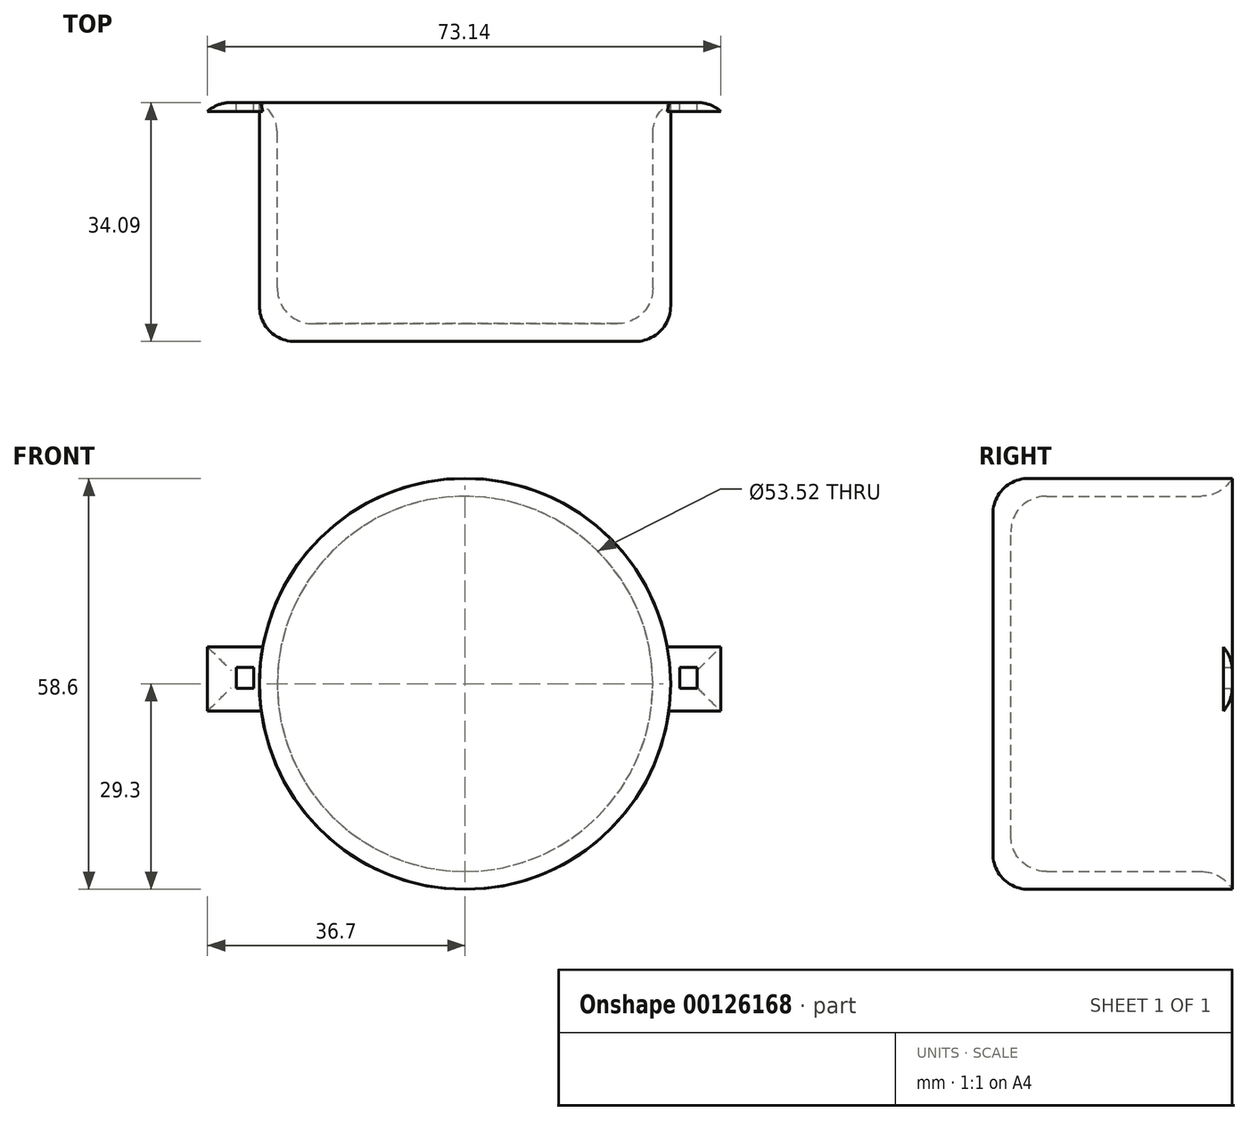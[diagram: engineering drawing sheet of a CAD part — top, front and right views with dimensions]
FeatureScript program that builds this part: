
annotation { "Feature Type Name" : "Feature", "Feature Type Description" : "" }
export const myFeature = defineFeature(function(context is Context, id is Id, definition is map)
    precondition{}
    {
        {
            var Q0;
            Q0=qCreatedBy(makeId("Front.planeOp"),FACE);
            var sketch = newSketch(context, id + "F0", { "sketchPlane" : qUnion([Q0])});
            skCircle(sketch, "E0", {"center": v(0, 0) * mm, "radius": 29.3 * mm});
            skLineSegment(sketch, "E1", {"start": v(28.82, 5.27) * mm, "end": v(36.44, 5.27) * mm});
            skLineSegment(sketch, "E2", {"start": v(36.44, 5.27) * mm, "end": v(36.44, -3.9) * mm});
            skLineSegment(sketch, "E3", {"start": v(36.44, -3.9) * mm, "end": v(29.04, -3.9) * mm});
            skLineSegment(sketch, "E4", {"start": v(-28.82, 5.27) * mm, "end": v(-36.7, 5.27) * mm});
            skLineSegment(sketch, "E5", {"start": v(-36.7, 5.27) * mm, "end": v(-36.7, -3.9) * mm});
            skLineSegment(sketch, "E6", {"start": v(-36.7, -3.9) * mm, "end": v(-29.04, -3.9) * mm});
            skLineSegment(sketch, "E7", {"start": v(30.6, 2.33) * mm, "end": v(30.6, -0.61) * mm});
            skLineSegment(sketch, "E8", {"start": v(30.6, -0.61) * mm, "end": v(33.06, -0.61) * mm});
            skLineSegment(sketch, "E9", {"start": v(33.06, -0.61) * mm, "end": v(33.06, 2.33) * mm});
            skLineSegment(sketch, "E10", {"start": v(33.06, 2.33) * mm, "end": v(30.6, 2.33) * mm});
            skLineSegment(sketch, "E11", {"start": v(-30.13, 2.33) * mm, "end": v(-32.6, 2.33) * mm});
            skLineSegment(sketch, "E12", {"start": v(-30.13, -0.61) * mm, "end": v(-32.6, -0.61) * mm});
            skLineSegment(sketch, "E13", {"start": v(-32.6, -0.61) * mm, "end": v(-32.6, 2.33) * mm});
            skLineSegment(sketch, "E14", {"start": v(-30.13, 2.33) * mm, "end": v(-30.13, -0.61) * mm});
            skSolve(sketch);
        }
        {
            var Q0;
            {var subQ0=sQuery(id+"F0.wireOp",EDGE,"E0");var subQ1=makeQuery(id+"F0.imprint","INTERSECT",VERTEX,{"derivedFrom":[subQ0,sQuery(id+"F0.wireOp",EDGE,"E1")]});Q0=makeQuery(id+"F0.imprint","IMPRINT",FACE,{"disambiguationData":[TD([[makeQuery(id+"F0.imprint","IMPRINT",EDGE,{"disambiguationData":[TD([[subQ1,-1.0]])],"derivedFrom":subQ0}),1.0]])]});}
            extrude(context, id + "F1", {"entities" : qUnion([Q0]), "depth" : 34.1 * mm});
        }
        {
            var Q0;
            Q0=makeQuery(id+"F1.opExtrude","CAP_FACE",FACE,{"disambiguationData":[OSD([sQuery(id+"F0.wireOp",EDGE,"E0")])],"isStart":true});
            shell(context, id + "F2", {"entities" : qUnion([Q0]), "thickness" : 2.54 * mm});
        }
        {
            var Q0;
            {var subQ0=sQuery(id+"F0.wireOp",EDGE,"E4");Q0=makeQuery(id+"F0.imprint","IMPRINT",FACE,{"disambiguationData":[TD([[makeQuery(id+"F0.imprint","IMPRINT",EDGE,{"derivedFrom":subQ0}),1.0]])]});}
            extrude(context, id + "F3", {"entities" : qUnion([Q0]), "depth" : 1.27 * mm});
        }
        {
            var Q0;
            {var subQ0=sQuery(id+"F0.wireOp",EDGE,"E1");Q0=makeQuery(id+"F0.imprint","IMPRINT",FACE,{"disambiguationData":[TD([[makeQuery(id+"F0.imprint","IMPRINT",EDGE,{"derivedFrom":subQ0}),-1.0]])]});}
            extrude(context, id + "F4", {"entities" : qUnion([Q0]), "depth" : 1.27 * mm});
        }
        {
            var Q0;
            Q0=makeQuery(id+"F1.opExtrude","CAP_EDGE",EDGE,{"disambiguationData":[OSD([sQuery(id+"F0.wireOp",EDGE,"E0")])],"isStart":false});
            var Q1;
            Q1=makeQuery(id+"F4.opExtrude","CAP_EDGE",EDGE,{"disambiguationData":[OSD([sQuery(id+"F0.wireOp",EDGE,"E2")])],"isStart":true});
            fillet(context, id + "F5", {"entities" : qUnion([Q0, Q1]), "radius" : 5.08 * mm, "tangentPropagation" : true, "allowEdgeOverflow" : false});
        }
        {
            var Q0;
            Q0=makeQuery(id+"F3.opExtrude","CAP_EDGE",EDGE,{"disambiguationData":[OSD([sQuery(id+"F0.wireOp",EDGE,"E5")])],"isStart":true});
            var Q1;
            {var subQ0=sQuery(id+"F0.wireOp",EDGE,"E0");Q1=makeQuery(id+"F2.opShell","OFFSET_EDGE",EDGE,{"disambiguationData":[OSD([subQ0]),TDD([makeQuery(id+"F1.opExtrude","CAP_EDGE",EDGE,{"disambiguationData":[OSD([subQ0])],"isStart":true})])]});}
            var Q2;
            {var subQ0=sQuery(id+"F0.wireOp",EDGE,"E0");Q2=makeQuery(id+"F2.opShell","OFFSET_EDGE",EDGE,{"disambiguationData":[OSD([subQ0]),TDD([makeQuery(id+"F1.opExtrude","CAP_EDGE",EDGE,{"disambiguationData":[OSD([subQ0])],"isStart":false})])]});}
            fillet(context, id + "F6", {"entities" : qUnion([Q0, Q1, Q2]), "radius" : 5.08 * mm, "tangentPropagation" : true, "allowEdgeOverflow" : false});
        }
        {
            var Q0;
            Q0=makeQuery(id+"F4.opExtrude","CAP_EDGE",EDGE,{"disambiguationData":[OSD([sQuery(id+"F0.wireOp",EDGE,"E3")])],"isStart":true});
            var Q1;
            Q1=makeQuery(id+"F4.opExtrude","CAP_EDGE",EDGE,{"disambiguationData":[OSD([sQuery(id+"F0.wireOp",EDGE,"E1")])],"isStart":true});
            var Q2;
            {var subQ0=sQuery(id+"F0.wireOp",EDGE,"E2");Q2=makeQuery(id+"F5.opFillet","BLEND_EDGE",EDGE,{"blendedFrom":[makeQuery(id+"F4.opExtrude","CAP_EDGE",EDGE,{"disambiguationData":[OSD([subQ0])],"isStart":true}),makeQuery(id+"F4.opExtrude","CAP_FACE",FACE,{"disambiguationData":[OSD([sQuery(id+"F0.wireOp",EDGE,"E0"),sQuery(id+"F0.wireOp",EDGE,"E1"),subQ0,sQuery(id+"F0.wireOp",EDGE,"E3"),sQuery(id+"F0.wireOp",EDGE,"E7"),sQuery(id+"F0.wireOp",EDGE,"E8"),sQuery(id+"F0.wireOp",EDGE,"E9"),sQuery(id+"F0.wireOp",EDGE,"E10")])],"isStart":true})],"blendedInto":[makeQuery(id+"F4.opExtrude","CAP_FACE",FACE,{"disambiguationData":[OSD([sQuery(id+"F0.wireOp",EDGE,"E0"),sQuery(id+"F0.wireOp",EDGE,"E1"),subQ0,sQuery(id+"F0.wireOp",EDGE,"E3"),sQuery(id+"F0.wireOp",EDGE,"E7"),sQuery(id+"F0.wireOp",EDGE,"E8"),sQuery(id+"F0.wireOp",EDGE,"E9"),sQuery(id+"F0.wireOp",EDGE,"E10")])],"isStart":true})]});}
            fillet(context, id + "F7", {"entities" : qUnion([Q0, Q1, Q2]), "radius" : 5.08 * mm, "tangentPropagation" : true, "allowEdgeOverflow" : false});
        }
        {
            var Q0;
            {var subQ0=sQuery(id+"F0.wireOp",EDGE,"E5");Q0=makeQuery(id+"F6.opFillet","BLEND_EDGE",EDGE,{"blendedFrom":[makeQuery(id+"F3.opExtrude","CAP_EDGE",EDGE,{"disambiguationData":[OSD([subQ0])],"isStart":true}),makeQuery(id+"F3.opExtrude","CAP_FACE",FACE,{"disambiguationData":[OSD([sQuery(id+"F0.wireOp",EDGE,"E0"),sQuery(id+"F0.wireOp",EDGE,"E4"),subQ0,sQuery(id+"F0.wireOp",EDGE,"E6"),sQuery(id+"F0.wireOp",EDGE,"E11"),sQuery(id+"F0.wireOp",EDGE,"E12"),sQuery(id+"F0.wireOp",EDGE,"E13"),sQuery(id+"F0.wireOp",EDGE,"E14")])],"isStart":true})],"blendedInto":[makeQuery(id+"F3.opExtrude","CAP_FACE",FACE,{"disambiguationData":[OSD([sQuery(id+"F0.wireOp",EDGE,"E0"),sQuery(id+"F0.wireOp",EDGE,"E4"),subQ0,sQuery(id+"F0.wireOp",EDGE,"E6"),sQuery(id+"F0.wireOp",EDGE,"E11"),sQuery(id+"F0.wireOp",EDGE,"E12"),sQuery(id+"F0.wireOp",EDGE,"E13"),sQuery(id+"F0.wireOp",EDGE,"E14")])],"isStart":true})]});}
            var Q1;
            Q1=makeQuery(id+"F3.opExtrude","CAP_EDGE",EDGE,{"disambiguationData":[OSD([sQuery(id+"F0.wireOp",EDGE,"E4")])],"isStart":true});
            var Q2;
            Q2=makeQuery(id+"F3.opExtrude","CAP_EDGE",EDGE,{"disambiguationData":[OSD([sQuery(id+"F0.wireOp",EDGE,"E6")])],"isStart":true});
            fillet(context, id + "F8", {"entities" : qUnion([Q0, Q1, Q2]), "radius" : 5.08 * mm, "tangentPropagation" : true, "allowEdgeOverflow" : false});
        }
    });
